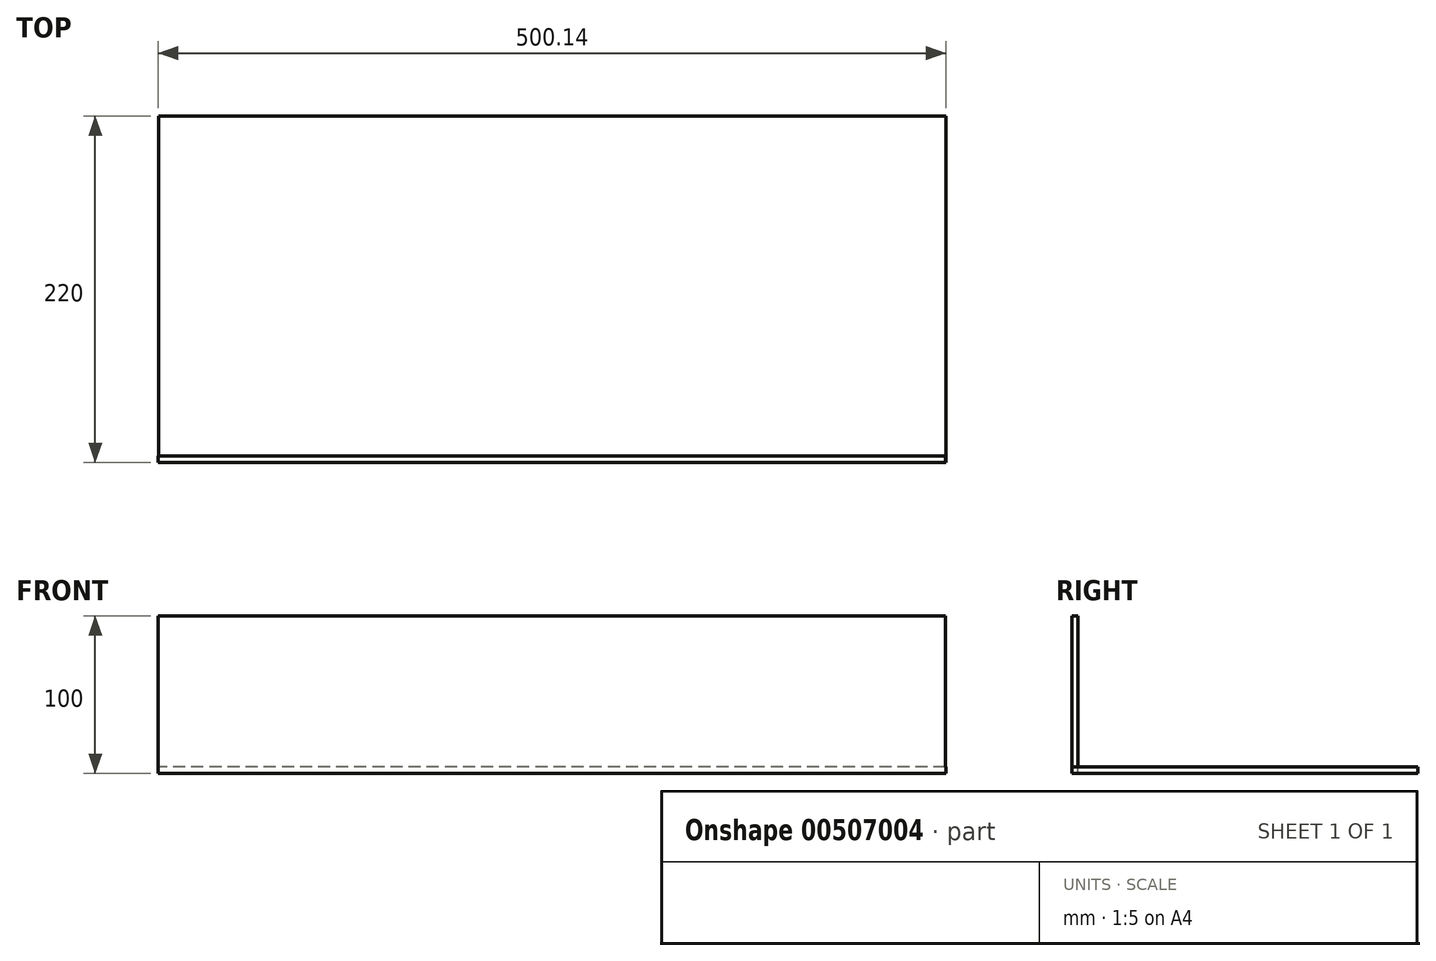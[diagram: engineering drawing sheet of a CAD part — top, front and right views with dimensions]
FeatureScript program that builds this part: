
annotation { "Feature Type Name" : "Feature", "Feature Type Description" : "" }
export const myFeature = defineFeature(function(context is Context, id is Id, definition is map)
    precondition{}
    {
        {
            var Q0;
            Q0=qCreatedBy(makeId("Top.planeOp"),FACE);
            var sketch = newSketch(context, id + "F0", { "sketchPlane" : qUnion([Q0])});
            skLineSegment(sketch, "E0.bottom", {"start": v(250, 110) * mm, "end": v(-250, 110) * mm});
            skLineSegment(sketch, "E0.top", {"start": v(250, -110) * mm, "end": v(-250, -110) * mm});
            skLineSegment(sketch, "E0.left", {"start": v(250, 110) * mm, "end": v(250, -110) * mm});
            skLineSegment(sketch, "E0.right", {"start": v(-250, 110) * mm, "end": v(-250, -110) * mm});
            skPoint(sketch, "E0.middle", {"position": v(0, 0) * mm});
            skSolve(sketch);
        }
        {
            var Q0;
            Q0=makeQuery(id+"F0.imprint","IMPRINT",FACE,{"disambiguationData":[TD([[makeQuery(id+"F0.imprint","IMPRINT",EDGE,{"derivedFrom":sQuery(id+"F0.wireOp",EDGE,"E0.bottom")}),1.0]])]});
            extrude(context, id + "F1", {"entities" : qUnion([Q0]), "depth" : 4 * mm});
        }
        {
            var Q0;
            Q0=qCreatedBy(makeId("Top.planeOp"),FACE);
            var sketch = newSketch(context, id + "F2", { "sketchPlane" : qUnion([Q0])});
            skLineSegment(sketch, "E1.bottom", {"start": v(-250.14, -110) * mm, "end": v(249.86, -110) * mm});
            skLineSegment(sketch, "E1.top", {"start": v(-250.14, -106) * mm, "end": v(249.86, -106) * mm});
            skLineSegment(sketch, "E1.left", {"start": v(-250.14, -110) * mm, "end": v(-250.14, -106) * mm});
            skLineSegment(sketch, "E1.right", {"start": v(249.86, -110) * mm, "end": v(249.86, -106) * mm});
            skSolve(sketch);
        }
        {
            var Q0;
            Q0 = qSketchRegion(id + "F2", true);
            extrude(context, id + "F3", {"entities" : qUnion([Q0]), "operationType" : NewBodyOperationType.ADD, "depth" : 100 * mm});
        }
    });
